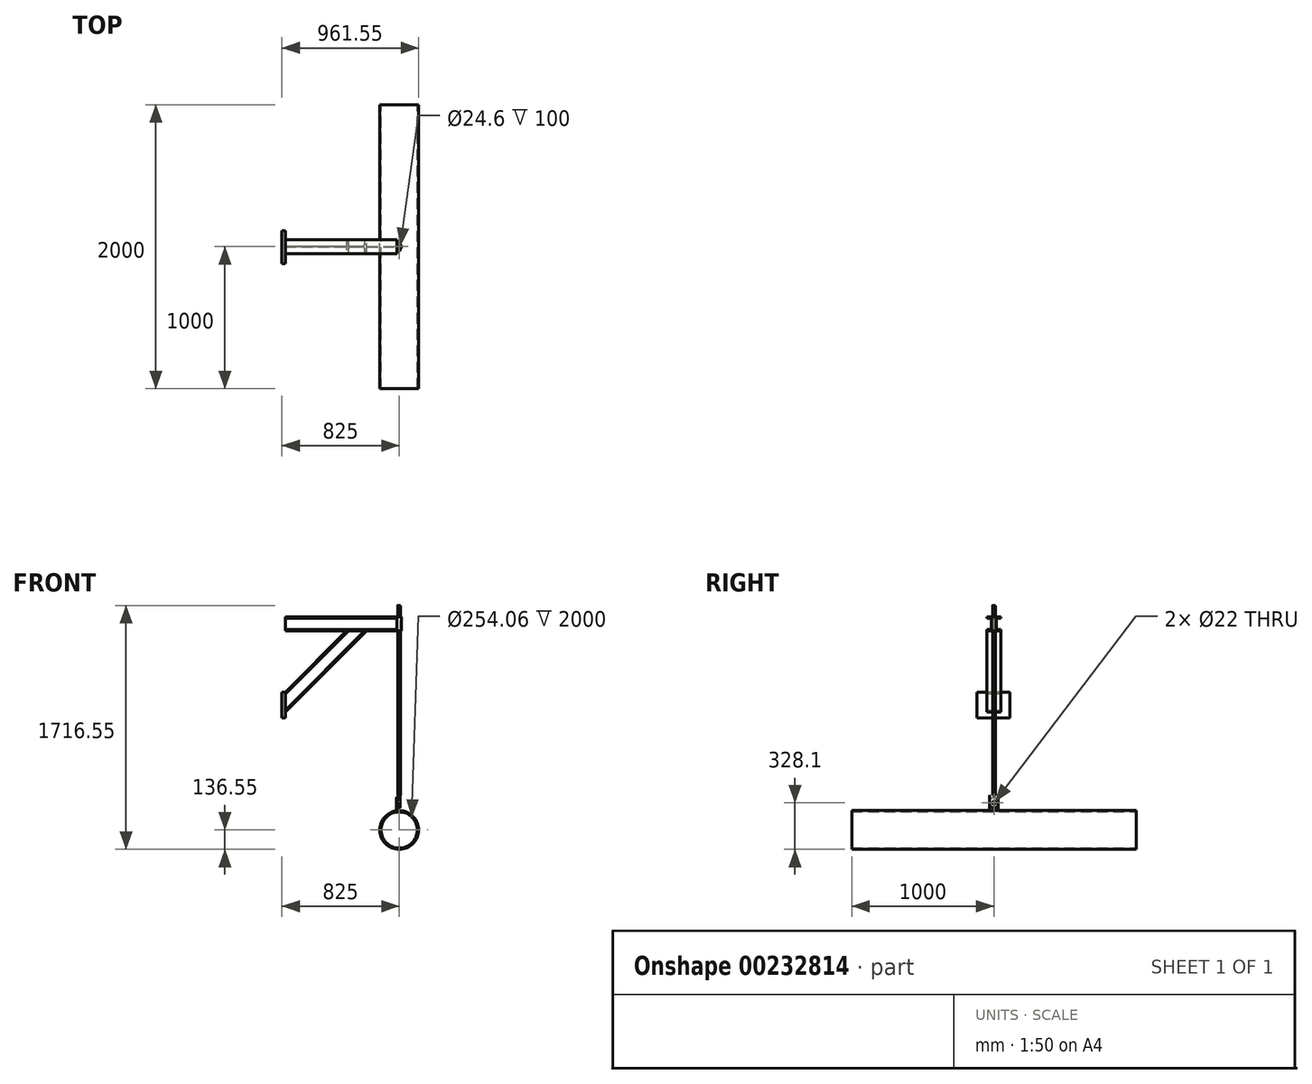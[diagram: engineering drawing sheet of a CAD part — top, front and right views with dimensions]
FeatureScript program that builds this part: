
annotation { "Feature Type Name" : "Feature", "Feature Type Description" : "" }
export const myFeature = defineFeature(function(context is Context, id is Id, definition is map)
    precondition{}
    {
        {
            var Q0;
            Q0=qCreatedBy(makeId("Right.planeOp"),FACE);
            var sketch = newSketch(context, id + "F0", { "sketchPlane" : qUnion([Q0])});
            skLineSegment(sketch, "E0", {"start": v(-50, 1500) * mm, "end": v(50, 1500) * mm});
            skLineSegment(sketch, "E1", {"start": v(50, 1500) * mm, "end": v(50, 1490) * mm});
            skLineSegment(sketch, "E2", {"start": v(50, 1490) * mm, "end": v(15, 1490) * mm});
            skLineSegment(sketch, "E3", {"start": v(3, 1478) * mm, "end": v(3, 1422) * mm});
            skLineSegment(sketch, "E4", {"start": v(15, 1410) * mm, "end": v(50, 1410) * mm});
            skLineSegment(sketch, "E5", {"start": v(50, 1410) * mm, "end": v(50, 1400) * mm});
            skLineSegment(sketch, "E6", {"start": v(50, 1400) * mm, "end": v(-50, 1400) * mm});
            skLineSegment(sketch, "E7", {"start": v(-50, 1400) * mm, "end": v(-50, 1410) * mm});
            skLineSegment(sketch, "E8", {"start": v(-50, 1410) * mm, "end": v(-15, 1410) * mm});
            skLineSegment(sketch, "E9", {"start": v(-3, 1422) * mm, "end": v(-3, 1478) * mm});
            skLineSegment(sketch, "E10", {"start": v(-15, 1490) * mm, "end": v(-50, 1490) * mm});
            skLineSegment(sketch, "E11", {"start": v(-50, 1490) * mm, "end": v(-50, 1500) * mm});
            skLineSegment(sketch, "E12", {"start": v(0, 1500) * mm, "end": v(0, 1400) * mm, "construction": true});
            skPoint(sketch, "E13.visualSharp", {"position": v(-3, 1490) * mm});
            skArc(sketch, "E13.filletArc", {"start": v(-3, 1478) * mm, "mid": v(-6.51, 1486.49) * mm, "end": v(-15, 1490) * mm});
            skPoint(sketch, "E14.visualSharp", {"position": v(3, 1490) * mm});
            skArc(sketch, "E14.filletArc", {"start": v(15, 1490) * mm, "mid": v(6.51, 1486.49) * mm, "end": v(3, 1478) * mm});
            skPoint(sketch, "E15.visualSharp", {"position": v(-3, 1410) * mm});
            skArc(sketch, "E15.filletArc", {"start": v(-15, 1410) * mm, "mid": v(-6.51, 1413.51) * mm, "end": v(-3, 1422) * mm});
            skPoint(sketch, "E16.visualSharp", {"position": v(3, 1410) * mm});
            skArc(sketch, "E16.filletArc", {"start": v(3, 1422) * mm, "mid": v(6.51, 1413.51) * mm, "end": v(15, 1410) * mm});
            skSolve(sketch);
        }
        {
            var Q0;
            Q0=makeQuery(id+"F0.imprint","IMPRINT",FACE,{"disambiguationData":[TD([[makeQuery(id+"F0.imprint","IMPRINT",EDGE,{"derivedFrom":sQuery(id+"F0.wireOp",EDGE,"E0")}),-1.0]])]});
            extrude(context, id + "F1", {"entities" : qUnion([Q0]), "oppositeDirection" : true, "depth" : 800 * mm, "hasSecondDirection" : true, "secondDirectionOppositeDirection" : true, "secondDirectionDepth" : (33.4 / 2) * mm});
        }
        {
            var Q0;
            Q0=makeQuery(id+"F1.opExtrude","SWEPT_FACE",FACE,{"disambiguationData":[OSD([sQuery(id+"F0.wireOp",EDGE,"E0")])]});
            var sketch = newSketch(context, id + "F2", { "sketchPlane" : qUnion([Q0])});
            skCircle(sketch, "E17", {"center": v(0, 0) * mm, "radius": 16.7 * mm});
            skCircle(sketch, "E18", {"center": v(0, 0) * mm, "radius": 12.3 * mm});
            skSolve(sketch);
        }
        {
            var Q0;
            Q0=makeQuery(id+"F2.imprint","IMPRINT",FACE,{"disambiguationData":[TD([[makeQuery(id+"F2.imprint","IMPRINT",EDGE,{"derivedFrom":sQuery(id+"F2.wireOp",EDGE,"E17")}),1.0]])]});
            var Q1;
            Q1=makeQuery(id+"F1.opExtrude","SWEPT_FACE",FACE,{"disambiguationData":[OSD([sQuery(id+"F0.wireOp",EDGE,"E6")])]});
            extrude(context, id + "F3", {"entities" : qUnion([Q0]), "operationType" : NewBodyOperationType.ADD, "endBound" : BoundingType.UP_TO_SURFACE, "oppositeDirection" : true, "endBoundEntityFace" : qUnion([Q1]), "depth" : 25 * mm});
        }
        {
            var Q0;
            Q0=qCreatedBy(makeId("Front.planeOp"),FACE);
            var sketch = newSketch(context, id + "F4", { "sketchPlane" : qUnion([Q0])});
            skCircle(sketch, "E19", {"center": v(0, 0) * mm, "radius": 136.55 * mm});
            skCircle(sketch, "E20", {"center": v(0, 0) * mm, "radius": 127.03 * mm});
            skSolve(sketch);
        }
        {
            var Q0;
            Q0=makeQuery(id+"F4.imprint","IMPRINT",FACE,{"disambiguationData":[TD([[makeQuery(id+"F4.imprint","IMPRINT",EDGE,{"derivedFrom":sQuery(id+"F4.wireOp",EDGE,"E19")}),1.0]])]});
            extrude(context, id + "F5", {"entities" : qUnion([Q0]), "endBound" : BoundingType.SYMMETRIC, "depth" : 2000 * mm});
        }
        {
            var Q0;
            Q0=qCreatedBy(makeId("Right.planeOp"),FACE);
            cPlane(context, id + "F6", {"entities" : qUnion([Q0]), "cplaneType" : CPlaneType.OFFSET, "offset" : 7 * mm, "oppositeDirection" : true, "width" : 150 * mm, "height" : 150 * mm});
        }
        {
            var Q0;
            Q0=qCreatedBy(id+"F6.planeOp",FACE);
            var sketch = newSketch(context, id + "F7", { "sketchPlane" : qUnion([Q0])});
            skLineSegment(sketch, "E21", {"start": v(-30, 136.55) * mm, "end": v(30, 136.55) * mm});
            skLineSegment(sketch, "E22", {"start": v(30, 136.55) * mm, "end": v(30, 198.55) * mm});
            skLineSegment(sketch, "E23", {"start": v(-30, 136.55) * mm, "end": v(-30, 198.55) * mm});
            skCircle(sketch, "E24", {"center": v(0, 191.55) * mm, "radius": 11 * mm});
            skLineSegment(sketch, "E25", {"start": v(0, 0) * mm, "end": v(-318.52, 0) * mm, "construction": true});
            skLineSegment(sketch, "E26", {"start": v(0, 191.55) * mm, "end": v(0, 0) * mm, "construction": true});
            skArc(sketch, "E27", {"start": v(-30, 198.55) * mm, "mid": v(0, 228.55) * mm, "end": v(30, 198.55) * mm});
            skSolve(sketch);
        }
        {
            var Q0;
            Q0=makeQuery(id+"F7.imprint","IMPRINT",FACE,{"disambiguationData":[TD([[makeQuery(id+"F7.imprint","IMPRINT",EDGE,{"derivedFrom":sQuery(id+"F7.wireOp",EDGE,"E21")}),1.0]])]});
            extrude(context, id + "F8", {"entities" : qUnion([Q0]), "oppositeDirection" : true, "depth" : 12 * mm});
        }
        {
            var Q0;
            Q0=makeQuery(id+"F1.opExtrude","SWEPT_FACE",FACE,{"disambiguationData":[OSD([sQuery(id+"F0.wireOp",EDGE,"E0")])]});
            var sketch = newSketch(context, id + "F9", { "sketchPlane" : qUnion([Q0])});
            skCircle(sketch, "E28", {"center": v(0, 0) * mm, "radius": 10 * mm});
            skSolve(sketch);
        }
        {
            var Q0;
            Q0=qCreatedBy(makeId("Right.planeOp"),FACE);
            var sketch = newSketch(context, id + "F10", { "sketchPlane" : qUnion([Q0])});
            skCircle(sketch, "E29", {"center": v(0, 191.55) * mm, "radius": 11 * mm});
            skArc(sketch, "E30", {"start": v(30, 184.55) * mm, "mid": v(0, 154.55) * mm, "end": v(-30, 184.55) * mm});
            skLineSegment(sketch, "E31", {"start": v(-30, 184.55) * mm, "end": v(-30, 246.55) * mm});
            skLineSegment(sketch, "E32", {"start": v(-30, 246.55) * mm, "end": v(30, 246.55) * mm});
            skLineSegment(sketch, "E33", {"start": v(30, 246.55) * mm, "end": v(30, 184.55) * mm});
            skLineSegment(sketch, "E34", {"start": v(0, 191.55) * mm, "end": v(0, 246.55) * mm, "construction": true});
            skSolve(sketch);
        }
        {
            var Q0;
            Q0=makeQuery(id+"F10.imprint","IMPRINT",FACE,{"disambiguationData":[TD([[makeQuery(id+"F10.imprint","IMPRINT",EDGE,{"derivedFrom":sQuery(id+"F10.wireOp",EDGE,"E29")}),-1.0]])]});
            extrude(context, id + "F11", {"entities" : qUnion([Q0]), "endBound" : BoundingType.SYMMETRIC, "depth" : 12 * mm});
        }
        {
            var Q0;
            Q0=makeQuery(id+"F9.imprint","IMPRINT",FACE,{"disambiguationData":[TD([[makeQuery(id+"F9.imprint","IMPRINT",EDGE,{"derivedFrom":sQuery(id+"F9.wireOp",EDGE,"E28")}),1.0]])]});
            var Q1;
            Q1=makeQuery(id+"F11.opExtrude","SWEPT_FACE",FACE,{"disambiguationData":[OSD([sQuery(id+"F10.wireOp",EDGE,"E32")])]});
            extrude(context, id + "F12", {"entities" : qUnion([Q0]), "endBound" : BoundingType.UP_TO_SURFACE, "oppositeDirection" : true, "endBoundEntityFace" : qUnion([Q1]), "depth" : 25 * mm, "hasSecondDirection" : true, "secondDirectionOppositeDirection" : false, "secondDirectionDepth" : 80 * mm});
        }
        {
            var Q0;
            Q0=qCreatedBy(makeId("Front.planeOp"),FACE);
            var sketch = newSketch(context, id + "F13", { "sketchPlane" : qUnion([Q0])});
            skLineSegment(sketch, "E35", {"start": v(-300, 1400) * mm, "end": v(-800, 900) * mm, "construction": true});
            skLineSegment(sketch, "E36", {"start": v(-800, 1400) * mm, "end": v(-550, 1150) * mm, "construction": true});
            skSolve(sketch);
        }
        {
            var Q0;
            Q0=sQuery(id+"F13.wireOp",EDGE,"E35");
            cPoint(context, id + "F14", {"entities" : qUnion([Q0]), "parameter" : 0.5});
        }
        {
            var Q0;
            Q0 = qCreatedBy(id + "F14" ,VERTEX);
            var Q1;
            Q1=sQuery(id+"F13.wireOp",EDGE,"E35");
            cPlane(context, id + "F15", {"entities" : qUnion([Q0, Q1]), "cplaneType" : CPlaneType.LINE_POINT, "offset" : 25 * mm, "width" : 150 * mm, "height" : 150 * mm});
        }
        {
            var Q0;
            Q0=qCreatedBy(id+"F15.planeOp",FACE);
            var sketch = newSketch(context, id + "F16", { "sketchPlane" : qUnion([Q0])});
            skLineSegment(sketch, "E37", {"start": v(50, 1152.08) * mm, "end": v(-50, 1152.08) * mm});
            skLineSegment(sketch, "E38", {"start": v(-50, 1152.08) * mm, "end": v(-50, 1162.08) * mm});
            skLineSegment(sketch, "E39", {"start": v(-50, 1162.08) * mm, "end": v(-15, 1162.08) * mm});
            skLineSegment(sketch, "E40", {"start": v(-3, 1174.08) * mm, "end": v(-3, 1230.08) * mm});
            skLineSegment(sketch, "E41", {"start": v(-15, 1242.08) * mm, "end": v(-50, 1242.08) * mm});
            skLineSegment(sketch, "E42", {"start": v(-50, 1242.08) * mm, "end": v(-50, 1252.08) * mm});
            skLineSegment(sketch, "E43", {"start": v(-50, 1252.08) * mm, "end": v(50, 1252.08) * mm});
            skLineSegment(sketch, "E44", {"start": v(50, 1252.08) * mm, "end": v(50, 1242.08) * mm});
            skLineSegment(sketch, "E45", {"start": v(50, 1242.08) * mm, "end": v(15, 1242.08) * mm});
            skLineSegment(sketch, "E46", {"start": v(3, 1230.08) * mm, "end": v(3, 1174.08) * mm});
            skLineSegment(sketch, "E47", {"start": v(15, 1162.08) * mm, "end": v(50, 1162.08) * mm});
            skLineSegment(sketch, "E48", {"start": v(50, 1162.08) * mm, "end": v(50, 1152.08) * mm});
            skPoint(sketch, "E49.visualSharp", {"position": v(3, 1242.08) * mm});
            skArc(sketch, "E49.filletArc", {"start": v(15, 1242.08) * mm, "mid": v(6.51, 1238.57) * mm, "end": v(3, 1230.08) * mm});
            skPoint(sketch, "E50.visualSharp", {"position": v(-3, 1242.08) * mm});
            skArc(sketch, "E50.filletArc", {"start": v(-3, 1230.08) * mm, "mid": v(-6.51, 1238.57) * mm, "end": v(-15, 1242.08) * mm});
            skPoint(sketch, "E51.visualSharp", {"position": v(-3, 1162.08) * mm});
            skArc(sketch, "E51.filletArc", {"start": v(-15, 1162.08) * mm, "mid": v(-6.51, 1165.6) * mm, "end": v(-3, 1174.08) * mm});
            skPoint(sketch, "E52.visualSharp", {"position": v(3, 1162.08) * mm});
            skArc(sketch, "E52.filletArc", {"start": v(3, 1174.08) * mm, "mid": v(6.51, 1165.6) * mm, "end": v(15, 1162.08) * mm});
            skLineSegment(sketch, "E53", {"start": v(0, 1252.08) * mm, "end": v(0, 1152.08) * mm, "construction": true});
            skSolve(sketch);
        }
        {
            var Q0;
            Q0=makeQuery(id+"F1.opExtrude","CAP_FACE",FACE,{"disambiguationData":[OSD([sQuery(id+"F0.wireOp",EDGE,"E0"),sQuery(id+"F0.wireOp",EDGE,"E1"),sQuery(id+"F0.wireOp",EDGE,"E2"),sQuery(id+"F0.wireOp",EDGE,"E3"),sQuery(id+"F0.wireOp",EDGE,"E4"),sQuery(id+"F0.wireOp",EDGE,"E5"),sQuery(id+"F0.wireOp",EDGE,"E6"),sQuery(id+"F0.wireOp",EDGE,"E7"),sQuery(id+"F0.wireOp",EDGE,"E8"),sQuery(id+"F0.wireOp",EDGE,"E9"),sQuery(id+"F0.wireOp",EDGE,"E10"),sQuery(id+"F0.wireOp",EDGE,"E11"),sQuery(id+"F0.wireOp",EDGE,"E13.filletArc"),sQuery(id+"F0.wireOp",EDGE,"E14.filletArc"),sQuery(id+"F0.wireOp",EDGE,"E15.filletArc"),sQuery(id+"F0.wireOp",EDGE,"E16.filletArc")])],"isStart":false});
            var sketch = newSketch(context, id + "F17", { "sketchPlane" : qUnion([Q0])});
            skLineSegment(sketch, "E54.bottom", {"start": v(-111.63, 970.94) * mm, "end": v(118.4, 970.94) * mm});
            skLineSegment(sketch, "E54.top", {"start": v(-111.63, 788.28) * mm, "end": v(118.4, 788.28) * mm});
            skLineSegment(sketch, "E54.left", {"start": v(-111.63, 970.94) * mm, "end": v(-111.63, 788.28) * mm});
            skLineSegment(sketch, "E54.right", {"start": v(118.4, 970.94) * mm, "end": v(118.4, 788.28) * mm});
            skSolve(sketch);
        }
        {
            var Q0;
            Q0=makeQuery(id+"F17.imprint","IMPRINT",FACE,{"disambiguationData":[TD([[makeQuery(id+"F17.imprint","IMPRINT",EDGE,{"derivedFrom":sQuery(id+"F17.wireOp",EDGE,"E54.bottom")}),-1.0]])]});
            extrude(context, id + "F18", {"entities" : qUnion([Q0]), "depth" : 25 * mm});
        }
        {
            var Q0;
            Q0=makeQuery(id+"F16.imprint","IMPRINT",FACE,{"disambiguationData":[TD([[makeQuery(id+"F16.imprint","IMPRINT",EDGE,{"derivedFrom":sQuery(id+"F16.wireOp",EDGE,"E37")}),-1.0]])]});
            var Q1;
            Q1=makeQuery(id+"F1.opExtrude","SWEPT_FACE",FACE,{"disambiguationData":[OSD([sQuery(id+"F0.wireOp",EDGE,"E6")])]});
            var Q2;
            Q2=makeQuery(id+"F18.opExtrude","CAP_FACE",FACE,{"disambiguationData":[OSD([sQuery(id+"F17.wireOp",EDGE,"E54.bottom"),sQuery(id+"F17.wireOp",EDGE,"E54.top"),sQuery(id+"F17.wireOp",EDGE,"E54.left"),sQuery(id+"F17.wireOp",EDGE,"E54.right")])],"isStart":true});
            extrude(context, id + "F19", {"entities" : qUnion([Q0]), "endBound" : BoundingType.UP_TO_SURFACE, "oppositeDirection" : true, "endBoundEntityFace" : qUnion([Q1]), "depth" : 25 * mm, "hasSecondDirection" : true, "secondDirectionBound" : SecondDirectionBoundingType.UP_TO_SURFACE, "secondDirectionOppositeDirection" : false, "secondDirectionBoundEntityFace" : qUnion([Q2]), "secondDirectionDepth" : 25 * mm});
        }
    });
